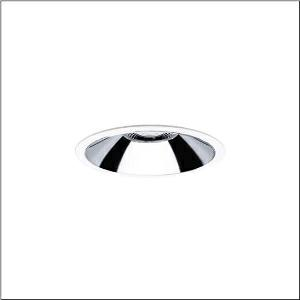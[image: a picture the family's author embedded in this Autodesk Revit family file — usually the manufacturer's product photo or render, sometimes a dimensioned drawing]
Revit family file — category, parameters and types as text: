
# Revit family: lunis_21_xl_51db15df32
name_source: partatom
category: Lighting Fixtures
units: mm (PartAtom-declared; Revit-internal decimal feet)

## family parameters
Cut with Voids When Loaded = No
Host = Face
Light Source = No
Part Type = Normal
Room Calculation Point = No
Round Connector Dimension = Use Diameter
Shared = No

## types (1)
- Lunis 21 XL (1 x LED, 2180 lm, 19.1 W, 3000K)
    Apparent Load = 19 VA
    CIE Flux Codes = 89 99 100 100 100
    Color Rendering = 80
    Color Temperature = 3000K
    Default Elevation = 1800 mm
    Description = Lunis 21,  XL, downlight, of PC, light emission: direct distribution, LED rated luminous flux: 2.180lm, light colour: 830, control gear: ECG DALI, with terminal, 5-pole, mains connection: 220..240V, AC, housing, round, of diecast aluminium, traffic white (RAL 9016), diameter: 213mm, protection rating (complete): IP20, protection rating (on room side): IP54, insulation class (complete): insulation class II (safety insulation), certification: CE, impact resistance: IK02, packaging unit: 1 piece
    Height = 0 mm  [stored 0 ft]
    Lamp = 1 x LED
    Lamp Light Flux = 2180 lm
    Lamp Power = 19.1 W
    Lamp count = 1
    Length = 213 mm
    Luminous efficacy = 114 lm/W
    Manufacturer = Siteco
    ModVariant = No
    Model = 51DB15DF32
    Mounting Place = Ceiling
    Mounting Type = Recessed
    Number of Poles = 1
    OnlyDefault = Yes
    Power Factor = 1
    Product Name = Lunis 21 XL
    Product group = downlight
    ProductGroupID = 400
    Protection Class = Protection class II
    Protection Degree = IP 20
    RLX_Detail_Level = 1
    RLX_Emergency_Light_Flux = 0 lm
    RLX_Emergency_Type = 0
    RLX_Emergency_Type_DB = No
    RlxData = <blob elided: 26953 chars, md5=7e6d4745>
    Socket = socket
    Standby Power = 0 W
    System Light Flux = 2180 lm
    System Power = 19 W
    Type Comments = Product without accessories
    Type Image = l_1287385.jpg
    URL = http://relux.com
    VarID = ---
    Voltage = 0 V
    Weight = 0.00 kg
    Width = 0 mm  [stored 0 ft]

note: [stored X ft] marks values corroborated as IEEE doubles in the binary element streams (Revit-internal decimal feet)

## geometry (parser evidence)
native form markers: Blend x4, Sweep x11
no freeform markers — native parametric forms only
